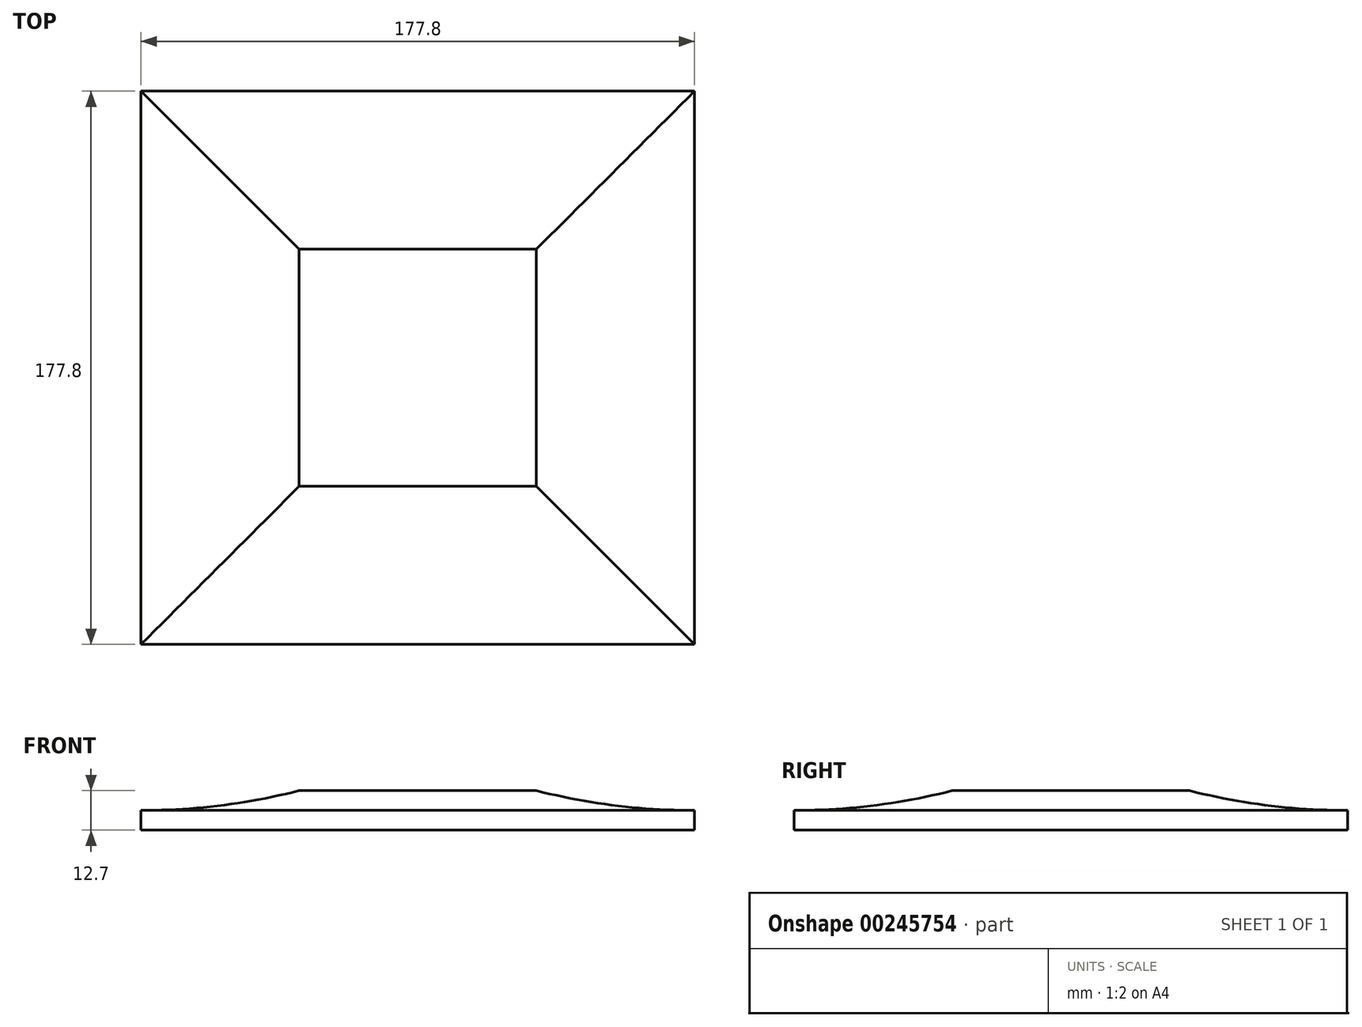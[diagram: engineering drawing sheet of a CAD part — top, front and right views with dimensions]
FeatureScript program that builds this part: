
annotation { "Feature Type Name" : "Feature", "Feature Type Description" : "" }
export const myFeature = defineFeature(function(context is Context, id is Id, definition is map)
    precondition{}
    {
        {
            var Q0;
            Q0=qCreatedBy(makeId("Front.planeOp"),FACE);
            var sketch = newSketch(context, id + "F0", { "sketchPlane" : qUnion([Q0])});
            skLineSegment(sketch, "E0", {"start": v(0, 0) * mm, "end": v(88.9, 0) * mm});
            skLineSegment(sketch, "E1", {"start": v(88.9, 0) * mm, "end": v(88.9, 6.35) * mm});
            skLineSegment(sketch, "E2", {"start": v(38.1, 12.7) * mm, "end": v(0, 12.7) * mm});
            skLineSegment(sketch, "E3", {"start": v(0, 12.7) * mm, "end": v(0, 0) * mm});
            skLineSegment(sketch, "E4", {"start": v(88.9, 6.35) * mm, "end": v(103.45, 6.35) * mm, "construction": true});
            skArc(sketch, "E5", {"start": v(88.9, 6.35) * mm, "mid": v(63.3, 7.94) * mm, "end": v(38.1, 12.7) * mm});
            skSolve(sketch);
        }
        {
            var Q0;
            Q0=qCreatedBy(makeId("Top.planeOp"),FACE);
            var sketch = newSketch(context, id + "F1", { "sketchPlane" : qUnion([Q0])});
            skLineSegment(sketch, "E6.bottom", {"start": v(-88.9, 88.9) * mm, "end": v(88.9, 88.9) * mm});
            skLineSegment(sketch, "E6.top", {"start": v(-88.9, -88.9) * mm, "end": v(88.9, -88.9) * mm});
            skLineSegment(sketch, "E6.left", {"start": v(-88.9, 88.9) * mm, "end": v(-88.9, -88.9) * mm});
            skLineSegment(sketch, "E6.right", {"start": v(88.9, 88.9) * mm, "end": v(88.9, -88.9) * mm});
            skPoint(sketch, "E6.middle", {"position": v(0, 0) * mm});
            skSolve(sketch);
        }
        {
            var Q0;
            Q0=makeQuery(id+"F0.imprint","IMPRINT",FACE,{"disambiguationData":[TD([[makeQuery(id+"F0.imprint","IMPRINT",EDGE,{"derivedFrom":sQuery(id+"F0.wireOp",EDGE,"E0")}),1.0]])]});
            var Q1;
            Q1=sQuery(id+"F1.wireOp",EDGE,"E6.right");
            var Q2;
            Q2=sQuery(id+"F1.wireOp",EDGE,"E6.bottom");
            var Q3;
            Q3=sQuery(id+"F1.wireOp",EDGE,"E6.left");
            var Q4;
            Q4=sQuery(id+"F1.wireOp",EDGE,"E6.top");
            sweep(context, id + "F2", {"profiles" : qUnion([Q0]), "path" : qUnion([Q1, Q2, Q3, Q4])});
        }
    });
